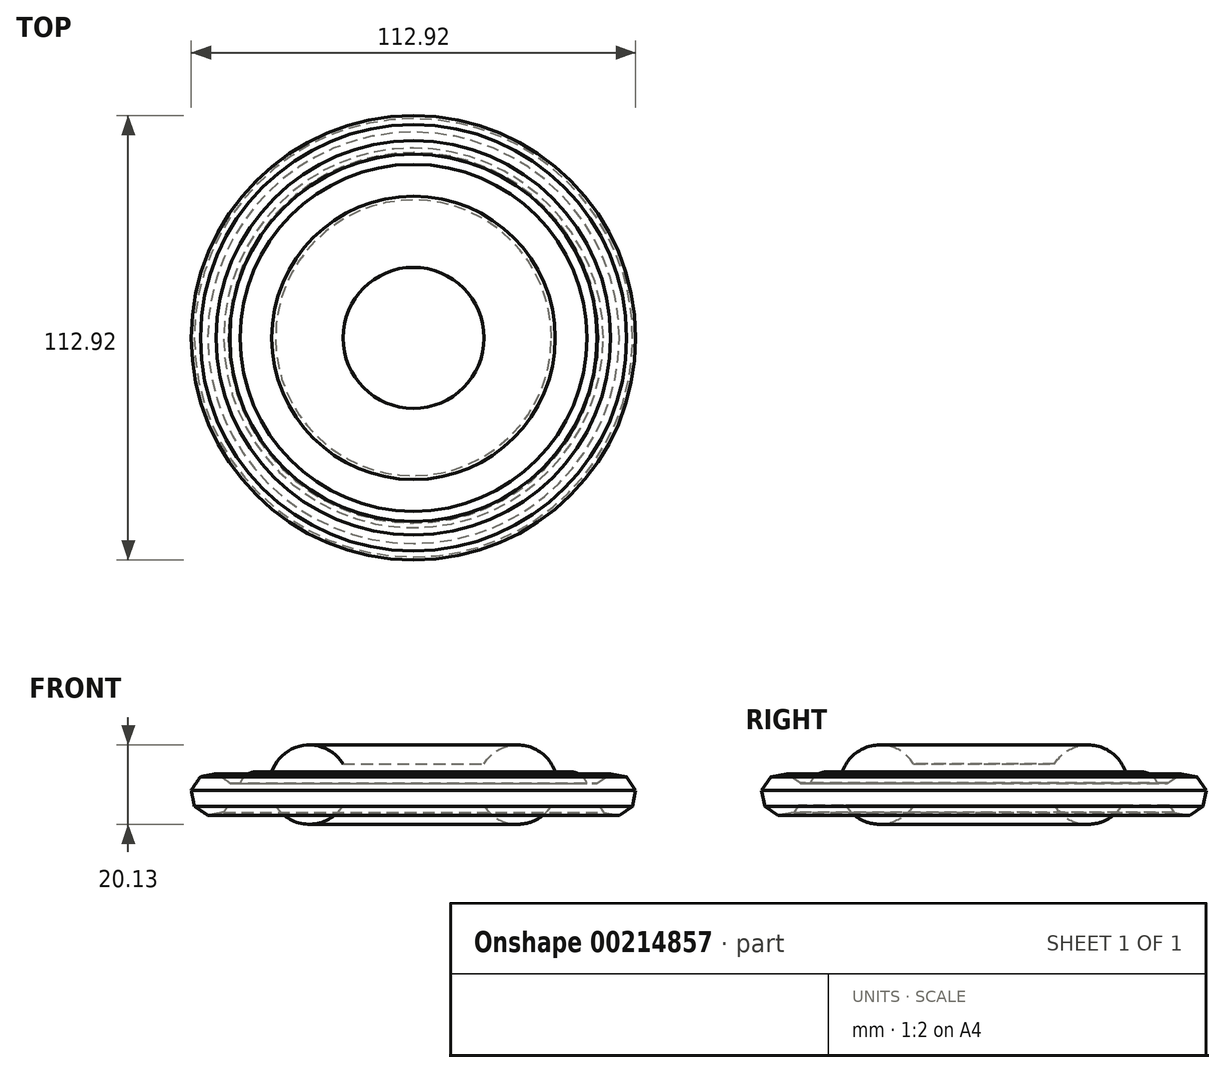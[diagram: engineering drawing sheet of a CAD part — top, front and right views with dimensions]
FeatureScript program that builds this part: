
annotation { "Feature Type Name" : "Feature", "Feature Type Description" : "" }
export const myFeature = defineFeature(function(context is Context, id is Id, definition is map)
    precondition{}
    {
        {
            var Q0;
            Q0=qCreatedBy(makeId("Front.planeOp"),FACE);
            var sketch = newSketch(context, id + "F0", { "sketchPlane" : qUnion([Q0])});
            skLineSegment(sketch, "E0.bottom", {"start": v(0, 0) * mm, "end": v(-32.95, 0) * mm});
            skLineSegment(sketch, "E0.top", {"start": v(0, 10.59) * mm, "end": v(-32.95, 10.59) * mm});
            skLineSegment(sketch, "E0.left", {"start": v(0, 0) * mm, "end": v(0, 10.59) * mm});
            skArc(sketch, "E1", {"start": v(-17.92, 10.59) * mm, "mid": v(-36.54, 5.3) * mm, "end": v(-17.92, 0) * mm});
            skPoint(sketch, "E1.centerSnap0", {"position": v(-32.95, 5.3) * mm});
            skSolve(sketch);
        }
        {
            var Q0;
            {var subQ0=sQuery(id+"F0.wireOp",EDGE,"E0.left");Q0=makeQuery(id+"F0.imprint","IMPRINT",FACE,{"disambiguationData":[TD([[makeQuery(id+"F0.imprint","IMPRINT",EDGE,{"derivedFrom":subQ0}),1.0]])]});}
            var Q1;
            Q1=sQuery(id+"F0.wireOp",EDGE,"E0.left");
            revolve(context, id + "F1", {"entities" : qUnion([Q0]), "axis" : qUnion([Q1]), "revolveType" : RevolveType.FULL});
        }
        {
            var Q0;
            Q0=qCreatedBy(makeId("Front.planeOp"),FACE);
            var sketch = newSketch(context, id + "F2", { "sketchPlane" : qUnion([Q0])});
            skLineSegment(sketch, "E2.bottom", {"start": v(0, 0) * mm, "end": v(-40, 0) * mm});
            skLineSegment(sketch, "E2.top", {"start": v(0, 8.53) * mm, "end": v(-40, 8.53) * mm});
            skLineSegment(sketch, "E2.left", {"start": v(0, 0) * mm, "end": v(0, 8.53) * mm});
            skLineSegment(sketch, "E2.right", {"start": v(-40, 0) * mm, "end": v(-40, 8.53) * mm});
            skArc(sketch, "E3", {"start": v(-40, 8.53) * mm, "mid": v(-44.27, 4.27) * mm, "end": v(-40, 0) * mm});
            skSolve(sketch);
        }
        {
            var Q0;
            Q0 = qSketchRegion(id + "F2", true);
            var Q1;
            Q1=sQuery(id+"F2.wireOp",EDGE,"E2.left");
            revolve(context, id + "F3", {"operationType" : NewBodyOperationType.ADD, "entities" : qUnion([Q0]), "axis" : qUnion([Q1]), "revolveType" : RevolveType.FULL});
        }
        {
            var Q0;
            Q0=qCreatedBy(makeId("Front.planeOp"),FACE);
            var sketch = newSketch(context, id + "F4", { "sketchPlane" : qUnion([Q0])});
            skLineSegment(sketch, "E4.bottom", {"start": v(0, 0) * mm, "end": v(-51.18, 0) * mm});
            skLineSegment(sketch, "E4.top", {"start": v(0, 5.59) * mm, "end": v(-51.18, 5.59) * mm});
            skLineSegment(sketch, "E4.left", {"start": v(0, 0) * mm, "end": v(0, 5.59) * mm});
            skLineSegment(sketch, "E4.right", {"start": v(-51.18, 0) * mm, "end": v(-51.18, 5.59) * mm});
            skCircle(sketch, "E5.cCircle", {"center": v(-51.18, 2.8) * mm, "radius": 4.98 * mm, "construction": true});
            skLineSegment(sketch, "E5.0", {"start": v(-45.9, 1.7) * mm, "end": v(-48.22, -1.7) * mm});
            skLineSegment(sketch, "E5.1", {"start": v(-48.22, -1.7) * mm, "end": v(-52.27, -2.48) * mm});
            skLineSegment(sketch, "E5.2", {"start": v(-52.27, -2.48) * mm, "end": v(-55.68, -0.17) * mm});
            skLineSegment(sketch, "E5.3", {"start": v(-55.68, -0.17) * mm, "end": v(-56.46, 3.88) * mm});
            skLineSegment(sketch, "E5.4", {"start": v(-56.46, 3.88) * mm, "end": v(-54.14, 7.3) * mm});
            skLineSegment(sketch, "E5.5", {"start": v(-54.14, 7.3) * mm, "end": v(-50.1, 8.07) * mm});
            skLineSegment(sketch, "E5.6", {"start": v(-50.1, 8.07) * mm, "end": v(-46.68, 5.76) * mm});
            skLineSegment(sketch, "E5.7", {"start": v(-46.68, 5.76) * mm, "end": v(-45.9, 1.7) * mm});
            skPoint(sketch, "E5.0.midPoint", {"position": v(-47.06, 0) * mm});
            skSolve(sketch);
        }
        {
            var Q0;
            Q0 = qSketchRegion(id + "F4", true);
            var Q1;
            Q1=sQuery(id+"F4.wireOp",EDGE,"E4.left");
            revolve(context, id + "F5", {"operationType" : NewBodyOperationType.ADD, "entities" : qUnion([Q0]), "axis" : qUnion([Q1]), "revolveType" : RevolveType.FULL});
        }
    });
